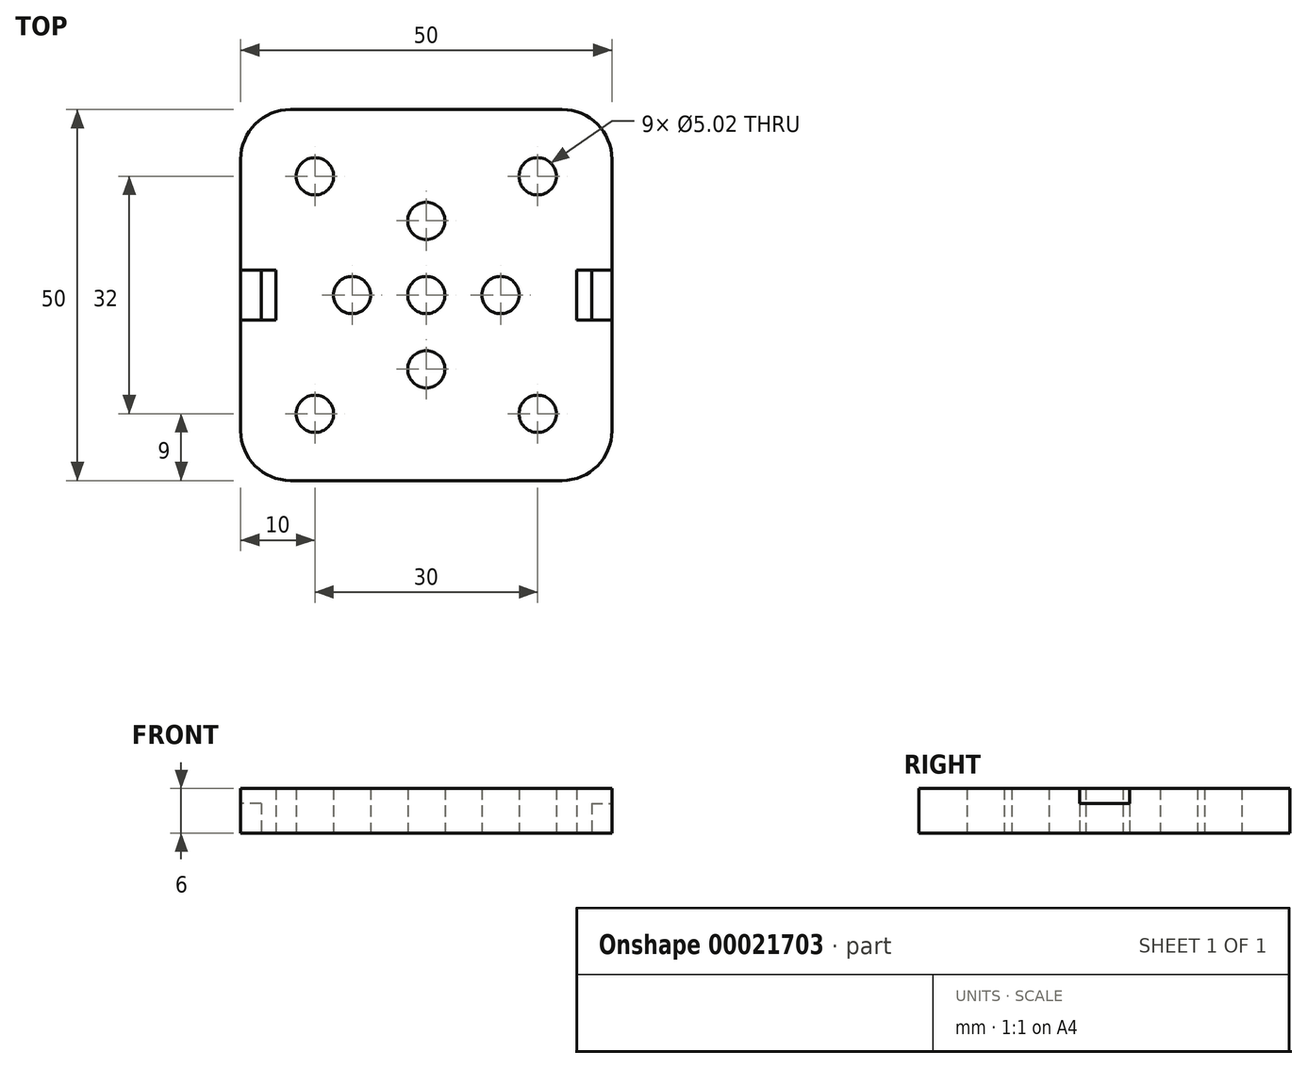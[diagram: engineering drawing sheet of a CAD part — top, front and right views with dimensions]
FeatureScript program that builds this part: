
annotation { "Feature Type Name" : "Feature", "Feature Type Description" : "" }
export const myFeature = defineFeature(function(context is Context, id is Id, definition is map)
    precondition{}
    {
        {
            var Q0;
            Q0=qCreatedBy(makeId("Top.planeOp"),FACE);
            var sketch = newSketch(context, id + "F1", { "sketchPlane" : qUnion([Q0])});
            skLineSegment(sketch, "E0", {"start": v(0, 0) * mm, "end": v(0, 25) * mm, "construction": true});
            skLineSegment(sketch, "E1", {"start": v(0, 0) * mm, "end": v(25, 0) * mm, "construction": true});
            skLineSegment(sketch, "E2", {"start": v(25, 0) * mm, "end": v(25, 18.3) * mm});
            skLineSegment(sketch, "E3", {"start": v(18.3, 25) * mm, "end": v(0, 25) * mm});
            skCircle(sketch, "E4", {"center": v(0, 0) * mm, "radius": 2.5 * mm, "construction": true});
            skLineSegment(sketch, "E5", {"start": v(15, 0) * mm, "end": v(15, 16) * mm, "construction": true});
            skLineSegment(sketch, "E6", {"start": v(15, 16) * mm, "end": v(0, 16) * mm, "construction": true});
            skCircle(sketch, "E7", {"center": v(15, 16) * mm, "radius": 2.5 * mm});
            skPoint(sketch, "E8.visualSharp", {"position": v(25, 25) * mm});
            skArc(sketch, "E8.filletArc", {"start": v(25, 18.3) * mm, "mid": v(23.04, 23.04) * mm, "end": v(18.3, 25) * mm});
            skLineSegment(sketch, "E9", {"start": v(22.26, 0) * mm, "end": v(22.26, 3.35) * mm});
            skLineSegment(sketch, "E10", {"start": v(22.26, 3.35) * mm, "end": v(25, 3.35) * mm});
            skLineSegment(sketch, "E11", {"start": v(22.26, 3.35) * mm, "end": v(20.26, 3.35) * mm});
            skLineSegment(sketch, "E12", {"start": v(20.26, 3.35) * mm, "end": v(20.26, 0) * mm});
            skCircle(sketch, "E13", {"center": v(10, 0) * mm, "radius": 2.5 * mm, "construction": true});
            skCircle(sketch, "E14", {"center": v(0, 10) * mm, "radius": 2.5 * mm, "construction": true});
            skLineSegment(sketch, "E15", {"start": v(10, 0) * mm, "end": v(0, 0) * mm, "construction": true});
            skLineSegment(sketch, "E16", {"start": v(0, 10) * mm, "end": v(0, 0) * mm, "construction": true});
            skArc(sketch, "E17", {"start": v(2.5, 0) * mm, "mid": v(1.77, 1.77) * mm, "end": v(0, 2.5) * mm});
            skArc(sketch, "E18", {"start": v(12.5, 0) * mm, "mid": v(10, 2.51) * mm, "end": v(7.5, 0) * mm});
            skArc(sketch, "E19", {"start": v(0, 7.5) * mm, "mid": v(2.5, 10) * mm, "end": v(0, 12.5) * mm});
            skArc(sketch, "E20.MirrorCS", {"start": v(0, 7.5) * mm, "mid": v(-2.5, 10) * mm, "end": v(0, 12.5) * mm});
            skArc(sketch, "E21.MirrorCS", {"start": v(-2.5, 0) * mm, "mid": v(-1.77, 1.77) * mm, "end": v(0, 2.5) * mm});
            skArc(sketch, "E22.MirrorCS", {"start": v(-12.5, 0) * mm, "mid": v(-10, 2.51) * mm, "end": v(-7.5, 0) * mm});
            skLineSegment(sketch, "E23.MirrorCS", {"start": v(-18.3, 25) * mm, "end": v(0, 25) * mm});
            skArc(sketch, "E24.MirrorCS", {"start": v(-25, 18.3) * mm, "mid": v(-23.04, 23.04) * mm, "end": v(-18.3, 25) * mm});
            skLineSegment(sketch, "E25.MirrorCS", {"start": v(-25, 0) * mm, "end": v(-25, 18.3) * mm});
            skLineSegment(sketch, "E26.MirrorCS", {"start": v(-22.26, 3.35) * mm, "end": v(-25, 3.35) * mm});
            skLineSegment(sketch, "E27.MirrorCS", {"start": v(-22.26, 0) * mm, "end": v(-22.26, 3.35) * mm});
            skLineSegment(sketch, "E28.MirrorCS", {"start": v(-22.26, 3.35) * mm, "end": v(-20.26, 3.35) * mm});
            skLineSegment(sketch, "E29.MirrorCS", {"start": v(-20.26, 3.35) * mm, "end": v(-20.26, 0) * mm});
            skCircle(sketch, "E30.MirrorC", {"center": v(-15, 16) * mm, "radius": 2.5 * mm});
            skLineSegment(sketch, "E31.MirrorCS", {"start": v(-25, 0) * mm, "end": v(-25, -18.3) * mm});
            skLineSegment(sketch, "E32.MirrorCS", {"start": v(-22.26, -3.35) * mm, "end": v(-25, -3.35) * mm});
            skLineSegment(sketch, "E33.MirrorCS", {"start": v(-22.26, 0) * mm, "end": v(-22.26, -3.35) * mm});
            skLineSegment(sketch, "E34.MirrorCS", {"start": v(-20.26, -3.35) * mm, "end": v(-20.26, 0) * mm});
            skLineSegment(sketch, "E35.MirrorCS", {"start": v(-22.26, -3.35) * mm, "end": v(-20.26, -3.35) * mm});
            skArc(sketch, "E36.MirrorCS", {"start": v(-12.5, 0) * mm, "mid": v(-10, -2.51) * mm, "end": v(-7.5, 0) * mm});
            skCircle(sketch, "E37.MirrorC", {"center": v(-15, -16) * mm, "radius": 2.5 * mm});
            skLineSegment(sketch, "E38.MirrorCS", {"start": v(-18.3, -25) * mm, "end": v(0, -25) * mm});
            skArc(sketch, "E39.MirrorCS", {"start": v(-25, -18.3) * mm, "mid": v(-23.04, -23.04) * mm, "end": v(-18.3, -25) * mm});
            skArc(sketch, "E40.MirrorCS", {"start": v(-2.5, 0) * mm, "mid": v(-1.77, -1.77) * mm, "end": v(0, -2.5) * mm});
            skArc(sketch, "E41.MirrorCS", {"start": v(2.5, 0) * mm, "mid": v(1.77, -1.77) * mm, "end": v(0, -2.5) * mm});
            skArc(sketch, "E42.MirrorCS", {"start": v(0, -7.5) * mm, "mid": v(2.5, -10) * mm, "end": v(0, -12.5) * mm});
            skArc(sketch, "E43.MirrorCS", {"start": v(0, -7.5) * mm, "mid": v(-2.5, -10) * mm, "end": v(0, -12.5) * mm});
            skArc(sketch, "E44.MirrorCS", {"start": v(12.5, 0) * mm, "mid": v(10, -2.51) * mm, "end": v(7.5, 0) * mm});
            skCircle(sketch, "E45.MirrorC", {"center": v(15, -16) * mm, "radius": 2.5 * mm});
            skLineSegment(sketch, "E46.MirrorCS", {"start": v(18.3, -25) * mm, "end": v(0, -25) * mm});
            skArc(sketch, "E47.MirrorCS", {"start": v(25, -18.3) * mm, "mid": v(23.04, -23.04) * mm, "end": v(18.3, -25) * mm});
            skLineSegment(sketch, "E48.MirrorCS", {"start": v(25, 0) * mm, "end": v(25, -18.3) * mm});
            skLineSegment(sketch, "E49.MirrorCS", {"start": v(20.26, -3.35) * mm, "end": v(20.26, 0) * mm});
            skLineSegment(sketch, "E50.MirrorCS", {"start": v(22.26, -3.35) * mm, "end": v(20.26, -3.35) * mm});
            skLineSegment(sketch, "E51.MirrorCS", {"start": v(22.26, 0) * mm, "end": v(22.26, -3.35) * mm});
            skLineSegment(sketch, "E52.MirrorCS", {"start": v(22.26, -3.35) * mm, "end": v(25, -3.35) * mm});
            skSolve(sketch);
        }
        {
            var Q0;
            Q0=makeQuery(id+"F1.imprint","IMPRINT",FACE,{"disambiguationData":[TD([[makeQuery(id+"F1.imprint","IMPRINT",EDGE,{"derivedFrom":sQuery(id+"F1.wireOp",EDGE,"E3")}),1.0]])]});
            extrude(context, id + "F0", {"entities" : qUnion([Q0]), "depth" : 6 * mm});
        }
        {
            var Q0;
            {var subQ4=sQuery(id+"F1.wireOp",EDGE,"E26.MirrorCS");Q0=makeQuery(id+"F1.imprint","IMPRINT",FACE,{"disambiguationData":[TD([[makeQuery(id+"F1.imprint","IMPRINT",EDGE,{"derivedFrom":subQ4}),1.0]])]});}
            var Q1;
            Q1=makeQuery(id+"F1.imprint","IMPRINT",FACE,{"disambiguationData":[TD([[makeQuery(id+"F1.imprint","IMPRINT",EDGE,{"derivedFrom":sQuery(id+"F1.wireOp",EDGE,"E9")}),-1.0]])]});
            extrude(context, id + "F2", {"entities" : qUnion([Q0, Q1]), "operationType" : NewBodyOperationType.ADD, "depth" : 4 * mm});
        }
    });
